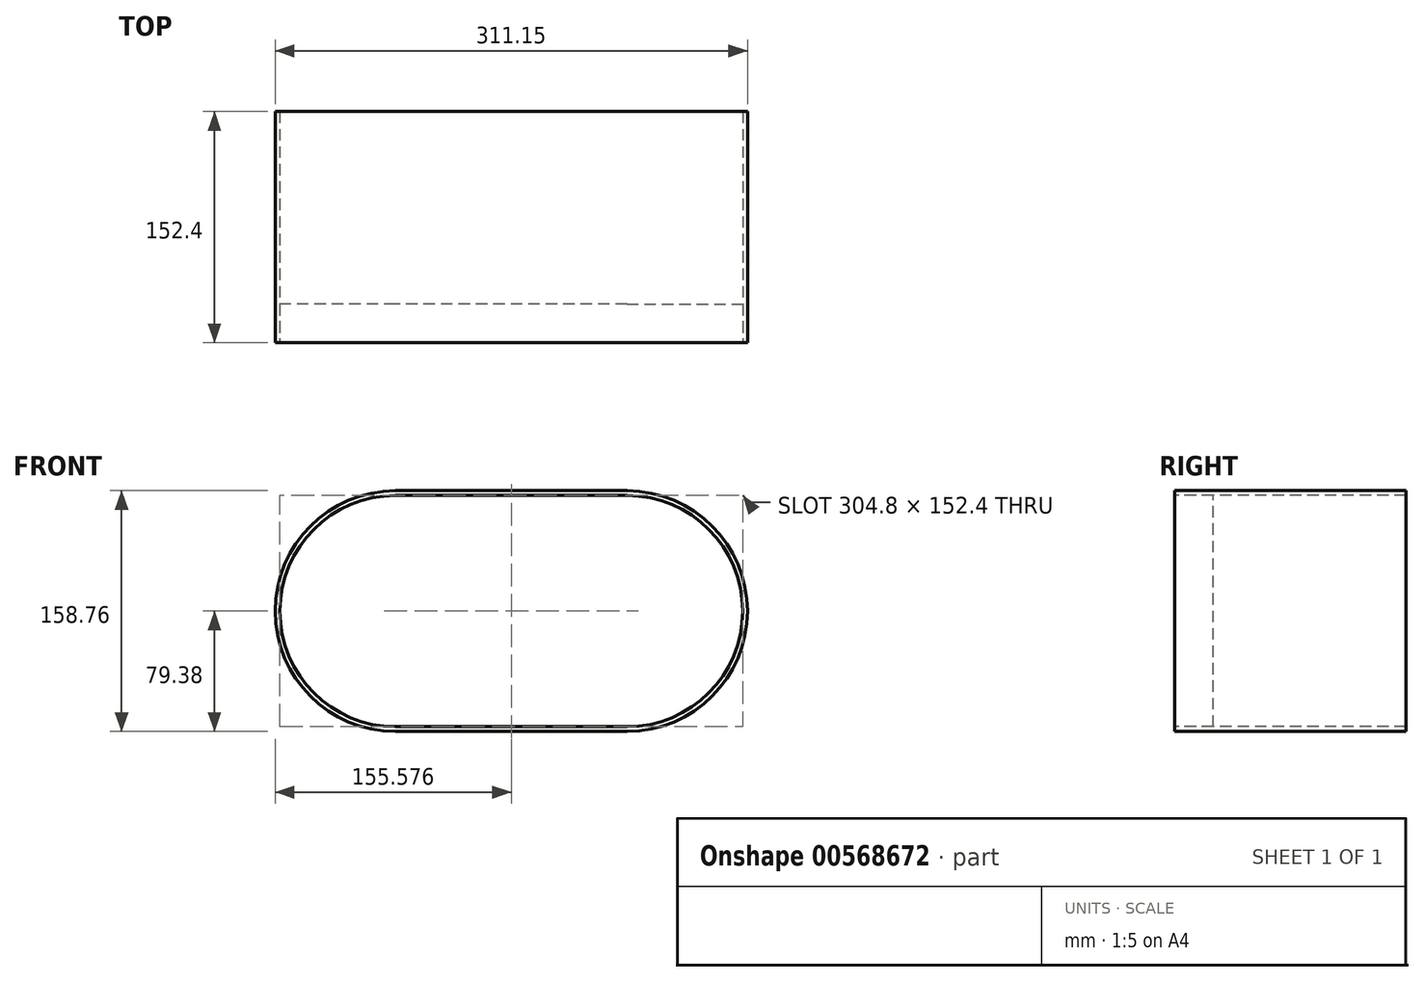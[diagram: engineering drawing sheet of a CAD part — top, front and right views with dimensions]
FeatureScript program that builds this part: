
annotation { "Feature Type Name" : "Feature", "Feature Type Description" : "" }
export const myFeature = defineFeature(function(context is Context, id is Id, definition is map)
    precondition{}
    {
        {
            var Q0;
            Q0=qCreatedBy(makeId("Front.planeOp"),FACE);
            var sketch = newSketch(context, id + "F0", { "sketchPlane" : qUnion([Q0])});
            skArc(sketch, "E0", {"start": v(-12.1, -76.2) * mm, "mid": v(64.1, 0) * mm, "end": v(-12.1, 76.2) * mm});
            skArc(sketch, "E1", {"start": v(-164.5, 76.2) * mm, "mid": v(-240.7, 0) * mm, "end": v(-164.5, -76.2) * mm});
            skLineSegment(sketch, "E2", {"start": v(-12.1, 76.2) * mm, "end": v(-164.5, 76.2) * mm});
            skLineSegment(sketch, "E3", {"start": v(-164.5, -76.2) * mm, "end": v(-12.1, -76.2) * mm});
            skArc(sketch, "E4", {"start": v(-12.1, -79.38) * mm, "mid": v(67.27, 0) * mm, "end": v(-12.1, 79.38) * mm});
            skArc(sketch, "E5", {"start": v(-164.5, 79.38) * mm, "mid": v(-243.88, 0) * mm, "end": v(-164.5, -79.38) * mm});
            skPoint(sketch, "E6.orphan", {"position": v(-12.1, 114.3) * mm});
            skLineSegment(sketch, "E7", {"start": v(-12.1, 79.38) * mm, "end": v(-164.5, 79.38) * mm});
            skLineSegment(sketch, "E8", {"start": v(-164.5, -79.38) * mm, "end": v(-12.1, -79.38) * mm});
            skSolve(sketch);
        }
        {
            var Q0;
            Q0 = qSketchRegion(id + "F0", true);
            extrude(context, id + "F1", {"entities" : qUnion([Q0]), "oppositeDirection" : true, "depth" : 152.4 * mm, "offsetDistance" : 25.4 * mm});
        }
        {
            var Q0;
            Q0=makeQuery(id+"F0.imprint","IMPRINT",FACE,{"disambiguationData":[TD([[makeQuery(id+"F0.imprint","IMPRINT",EDGE,{"derivedFrom":sQuery(id+"F0.wireOp",EDGE,"E0")}),1.0]])]});
            extrude(context, id + "F2", {"entities" : qUnion([Q0]), "oppositeDirection" : true, "depth" : 25.4 * mm, "offsetDistance" : 25.4 * mm});
        }
    });
